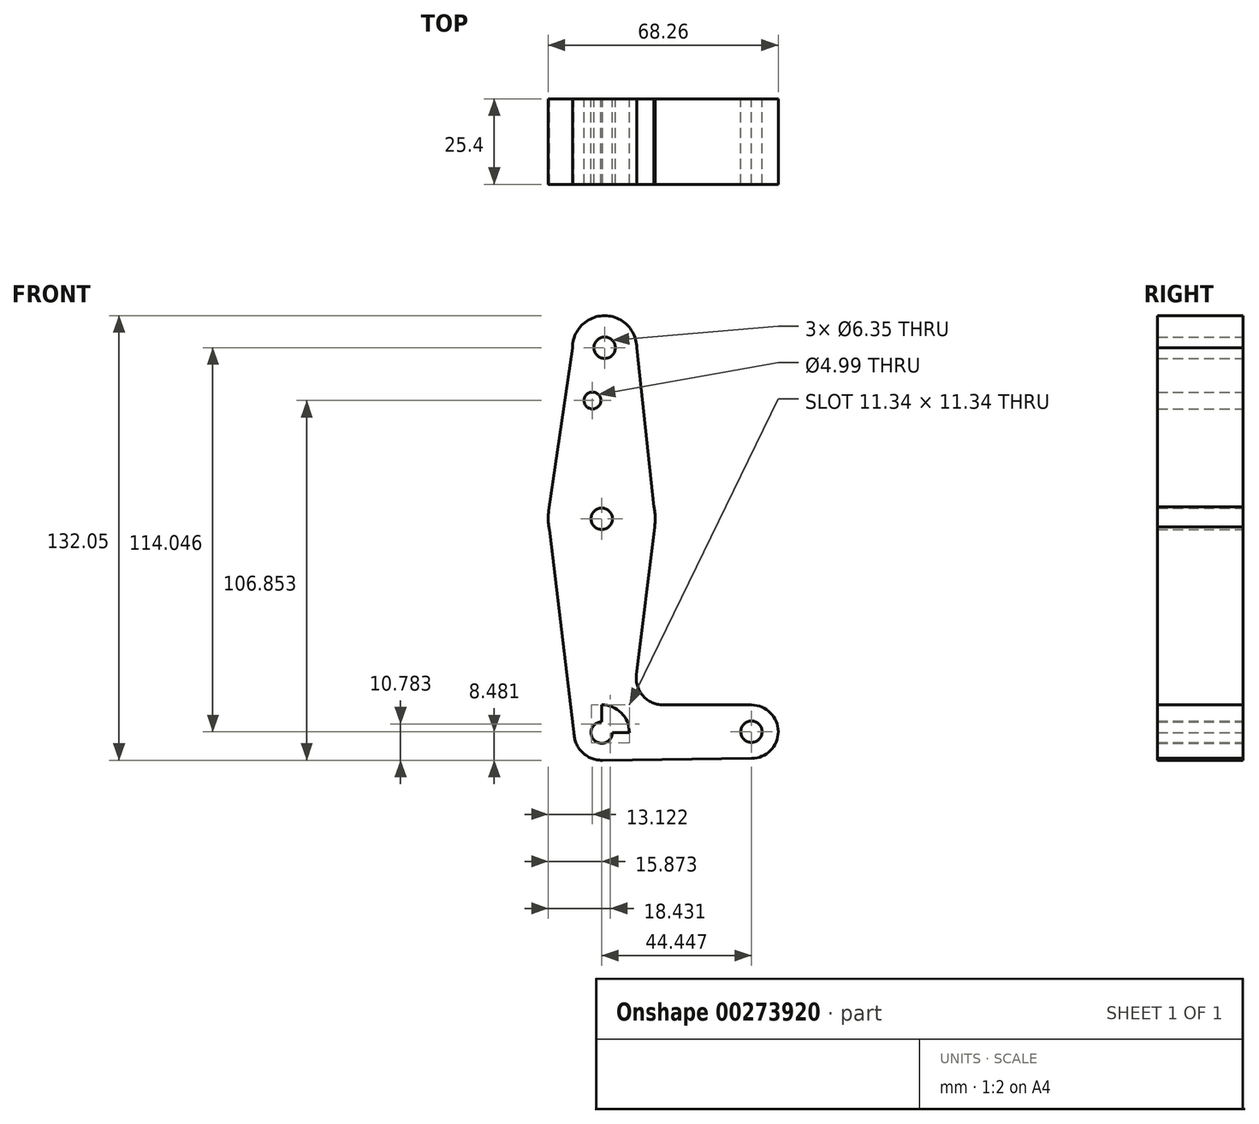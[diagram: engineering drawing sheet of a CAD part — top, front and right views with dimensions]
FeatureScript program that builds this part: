
annotation { "Feature Type Name" : "Feature", "Feature Type Description" : "" }
export const myFeature = defineFeature(function(context is Context, id is Id, definition is map)
    precondition{}
    {
        {
            var Q0;
            Q0=qCreatedBy(makeId("Front.planeOp"),FACE);
            var sketch = newSketch(context, id + "F0", { "sketchPlane" : qUnion([Q0])});
            skCircle(sketch, "E0", {"center": v(-43.58, 41.89) * mm, "radius": 9.53 * mm});
            skCircle(sketch, "E1", {"center": v(-44.45, -8.91) * mm, "radius": 15.88 * mm});
            skCircle(sketch, "E2", {"center": v(-44.45, -72.41) * mm, "radius": 8.23 * mm});
            skCircle(sketch, "E3", {"center": v(0, -72.16) * mm, "radius": 7.94 * mm});
            skLineSegment(sketch, "E4", {"start": v(-43.58, 41.89) * mm, "end": v(-44.45, -8.91) * mm});
            skLineSegment(sketch, "E5", {"start": v(-44.45, -8.91) * mm, "end": v(-44.45, -72.41) * mm});
            skLineSegment(sketch, "E6", {"start": v(-44.45, -72.41) * mm, "end": v(0, -72.16) * mm});
            skPoint(sketch, "E7", {"position": v(-53.1, 41.81) * mm});
            skPoint(sketch, "E8", {"position": v(-34.06, 41.82) * mm});
            skPoint(sketch, "E9", {"position": v(-60.17, -6.72) * mm});
            skPoint(sketch, "E10", {"position": v(-28.98, -5.35) * mm});
            skPoint(sketch, "E11", {"position": v(-28.64, -10.34) * mm});
            skPoint(sketch, "E12", {"position": v(-59.99, -12.15) * mm});
            skPoint(sketch, "E13", {"position": v(-52.67, -72.41) * mm});
            skPoint(sketch, "E14", {"position": v(-36.22, -72.37) * mm});
            skPoint(sketch, "E15", {"position": v(-44.45, -80.64) * mm});
            skPoint(sketch, "E16", {"position": v(-44.45, -64.19) * mm});
            skPoint(sketch, "E17", {"position": v(0, -64.22) * mm});
            skPoint(sketch, "E18", {"position": v(0, -80.1) * mm});
            skLineSegment(sketch, "E19", {"start": v(-60.17, -6.72) * mm, "end": v(-53.1, 41.81) * mm});
            skLineSegment(sketch, "E20", {"start": v(-28.98, -5.35) * mm, "end": v(-34.06, 41.82) * mm});
            skLineSegment(sketch, "E21", {"start": v(-28.64, -10.34) * mm, "end": v(-34.13, -55.28) * mm});
            skLineSegment(sketch, "E22", {"start": v(-59.99, -12.15) * mm, "end": v(-52.67, -72.41) * mm});
            skLineSegment(sketch, "E23", {"start": v(-44.45, -80.64) * mm, "end": v(0, -80.1) * mm});
            skLineSegment(sketch, "E24", {"start": v(-26.25, -64.2) * mm, "end": v(0, -64.22) * mm});
            skCircle(sketch, "E25", {"center": v(-43.58, 41.89) * mm, "radius": 3.18 * mm});
            skCircle(sketch, "E26", {"center": v(-44.45, -8.91) * mm, "radius": 3.18 * mm});
            skCircle(sketch, "E27", {"center": v(-44.45, -72.41) * mm, "radius": 3.18 * mm});
            skCircle(sketch, "E28", {"center": v(0, -72.16) * mm, "radius": 3.18 * mm});
            skCircle(sketch, "E29", {"center": v(-47.2, 26.21) * mm, "radius": 2.5 * mm});
            skArc(sketch, "E30.filletArc", {"start": v(-34.13, -55.28) * mm, "mid": v(-32.2, -61.52) * mm, "end": v(-26.25, -64.2) * mm});
            skSolve(sketch);
        }
        {
            var Q0;
            Q0 = qSketchRegion(id + "F0", true);
            extrude(context, id + "F1", {"entities" : qUnion([Q0]), "depth" : 25.4 * mm});
        }
    });
